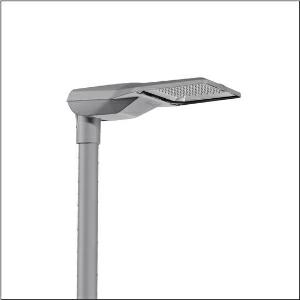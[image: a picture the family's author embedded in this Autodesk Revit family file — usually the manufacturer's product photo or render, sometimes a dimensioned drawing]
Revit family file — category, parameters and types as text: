
# Revit family: streetlight_sl_21_iq_midi___st1_0a_5xe3d41g08mb_322d
name_source: partatom
category: Lighting Fixtures
units: mm (PartAtom-declared; Revit-internal decimal feet)

## family parameters
Cut with Voids When Loaded = No
Host = Face
Light Source = No
Part Type = Normal
Room Calculation Point = No
Round Connector Dimension = Use Diameter
Shared = No

## types (1)
- --- (1 x LED, 20360 lm, 146.7 W, 4000K)
    Apparent Load = 147 VA
    CIE Flux Codes = 37 72 97 100 100
    Color Rendering = 70
    Color Temperature = 4000K
    Default Elevation = 1800 mm
    Description = Streetlight SL 21 iQ midi, mast luminaire, primary light control with lens, of PMMA, primary optical cover: cover, of toughened safety glass, transparent, light distribution: ST1.0a, light emission: direct distribution, primary light characteristic: asymmetric, installation type: post-top, side-entry, LED, High Power LED, rated luminous flux: 20.360lm, luminous efficacy: 139lm/W, light colour: 740, colour temperature: 4000K, control: Street-Remote, Auto-Match, Temp-Guard, Lumen-Switch, Night-Set, Smart-Wire, Light-Fading, Desk-Remote (wireless, voltage-free reading and setting of iQ features in the workshop via application-optimized NFC function/RFID function), optimised constant luminous flux control (CLO 2.0), presetting dimming linear, mains connection: 230..240V, AC, 50/60Hz, start of lifetime: 147W, end of service life: 161W, reduction: 62W, luminaire housing, of diecast aluminium, powder-coated, Siteco® metallic grey (DB 702S), corrosivity category C5 mid according to DIN EN ISO 12944, please order mast flange separately, inclination adjustable: 0°, 5°, 10°, 15°, sealing non-destructively replaceable, multi-level sealing system, length: 644mm, width: 335mm, height: 110mm, mast flange for spigot size: 42mm (side-entry): 5XC10008XM4, 60/48mm (side-entry/post-top): 5XC10108XM2, 76/60mm (side-entry/post-top): 5XC10108XM1, protection rating (complete): IP66, insulation class (complete): insulation class II (safety insulation), certification: CE, ENEC, ENEC+, VDE, impact resistance: IK09, permissible operating ambient temperature for outdoor applications: -40..+50°C, standard-compliant lighting for roads and squares, packaging unit: 1 piece

Light Distribution: ST1.0a
    Height = 111 mm
    Lamp = 1 x LED
    Lamp Light Flux = 20360 lm
    Lamp Power = 146.7 W
    Lamp count = 1
    Length = 644 mm
    Luminous efficacy = 139 lm/W
    Manufacturer = Siteco
    ModVariant = No
    Model = 5XE3D41G08MB
    Number of Poles = 1
    OnlyDefault = Yes
    Power Factor = 1
    Product Name = Streetlight SL 21 iQ midi | ST1.0a
    Product group = mast luminaire | pylon top
    ProductGroupID = 6100
    Protection Class = Protection class II
    Protection Degree = IP 66
    RLX_Detail_Level = 1
    RLX_Emergency_Light_Flux = 0 lm
    RLX_Emergency_Type = 0
    RLX_Emergency_Type_DB = No
    RlxData = <blob elided: 90837 chars, md5=0c4f8fee>
    Socket = socket
    Standby Power = 0 W
    System Light Flux = 20360 lm
    System Power = 147 W
    Type Comments = factory setting: luminous flux: 100 % | dim-lin: 254 | 753 mA
    Type Image = l_1004298.jpg
    URL = http://relux.com
    VarID = @adj_141743
    Voltage = 0 V
    Weight = 0.00 kg
    Width = 336 mm

## geometry (parser evidence)
native form markers: Blend x4, Sweep x11
no freeform markers — native parametric forms only
